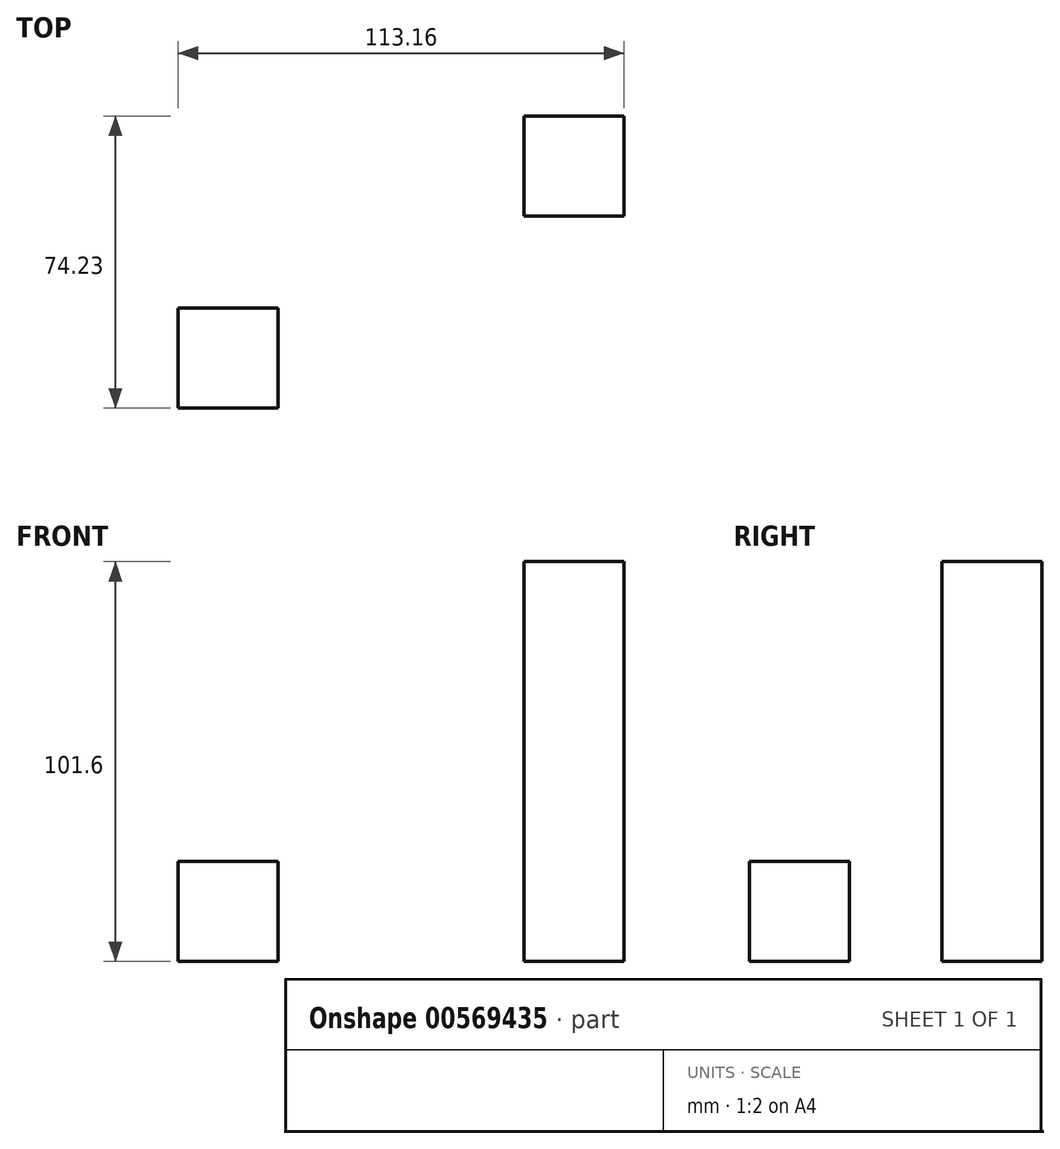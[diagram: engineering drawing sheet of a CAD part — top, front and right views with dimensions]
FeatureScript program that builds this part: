
annotation { "Feature Type Name" : "Feature", "Feature Type Description" : "" }
export const myFeature = defineFeature(function(context is Context, id is Id, definition is map)
    precondition{}
    {
        {
            var Q0;
            Q0=qCreatedBy(makeId("Front.planeOp"),FACE);
            var sketch = newSketch(context, id + "F0", { "sketchPlane" : qUnion([Q0])});
            skLineSegment(sketch, "E0.bottom", {"start": v(-34.52, 25.4) * mm, "end": v(-9.12, 25.4) * mm});
            skLineSegment(sketch, "E0.top", {"start": v(-34.52, 0) * mm, "end": v(-9.12, 0) * mm});
            skLineSegment(sketch, "E0.left", {"start": v(-34.52, 25.4) * mm, "end": v(-34.52, 0) * mm});
            skLineSegment(sketch, "E0.right", {"start": v(-9.12, 25.4) * mm, "end": v(-9.12, 0) * mm});
            skSolve(sketch);
        }
        {
            var Q0;
            Q0=makeQuery(id+"F0.imprint","IMPRINT",FACE,{"disambiguationData":[TD([[makeQuery(id+"F0.imprint","IMPRINT",EDGE,{"derivedFrom":sQuery(id+"F0.wireOp",EDGE,"E0.bottom")}),-1.0]])]});
            extrude(context, id + "F1", {"entities" : qUnion([Q0]), "depth" : 25.4 * mm, "offsetDistance" : 25.4 * mm});
        }
        {
            var Q0;
            Q0=qCreatedBy(makeId("Top.planeOp"),FACE);
            var sketch = newSketch(context, id + "F2", { "sketchPlane" : qUnion([Q0])});
            skLineSegment(sketch, "E1.bottom", {"start": v(78.64, 23.43) * mm, "end": v(53.24, 23.43) * mm});
            skLineSegment(sketch, "E1.top", {"start": v(78.64, 48.83) * mm, "end": v(53.24, 48.83) * mm});
            skLineSegment(sketch, "E1.left", {"start": v(78.64, 23.43) * mm, "end": v(78.64, 48.83) * mm});
            skLineSegment(sketch, "E1.right", {"start": v(53.24, 23.43) * mm, "end": v(53.24, 48.83) * mm});
            skSolve(sketch);
        }
        {
            var Q0;
            Q0 = qSketchRegion(id + "F2", true);
            extrude(context, id + "F3", {"entities" : qUnion([Q0]), "depth" : 101.6 * mm, "offsetDistance" : 25.4 * mm});
        }
    });
